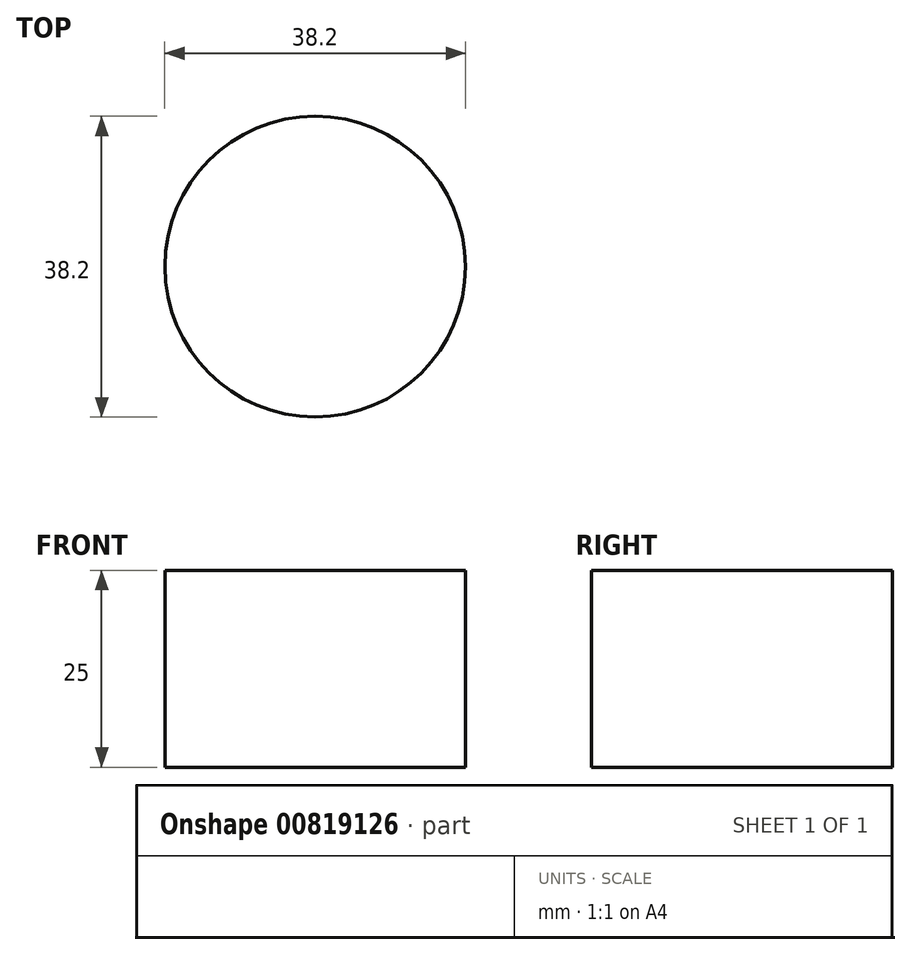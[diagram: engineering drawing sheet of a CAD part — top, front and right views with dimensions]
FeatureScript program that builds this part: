
annotation { "Feature Type Name" : "Feature", "Feature Type Description" : "" }
export const myFeature = defineFeature(function(context is Context, id is Id, definition is map)
    precondition{}
    {
        {
            var Q0;
            Q0=qCreatedBy(makeId("Top.planeOp"),FACE);
            var sketch = newSketch(context, id + "F0", { "sketchPlane" : qUnion([Q0])});
            skCircle(sketch, "E0", {"center": v(0, 0) * mm, "radius": 19.1 * mm});
            skSolve(sketch);
        }
        {
            var Q0;
            Q0=makeQuery(id+"F0.imprint","IMPRINT",FACE,{"disambiguationData":[TD([[makeQuery(id+"F0.imprint","IMPRINT",EDGE,{"derivedFrom":sQuery(id+"F0.wireOp",EDGE,"E0")}),1.0]])]});
            extrude(context, id + "F1", {"entities" : qUnion([Q0]), "depth" : 25 * mm, "offsetDistance" : 25 * mm});
        }
    });
